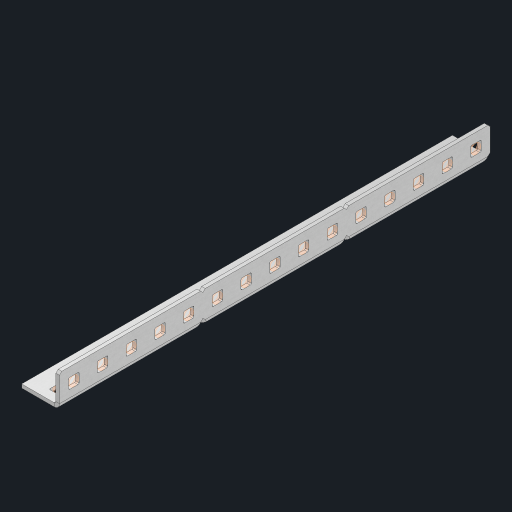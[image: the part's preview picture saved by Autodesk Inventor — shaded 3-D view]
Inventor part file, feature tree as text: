
AUTODESK INVENTOR PART (.ipt)
format: ipt  version: 2023 (Build 270158000, 158)  size: 680,960 bytes
history: native  units: in
note: dims shown in document units (in); Inventor stores cm internally (conversion verified against a paired STEP export)
features: other x35, extrude x29, sheet_metal_op x10, sketch x8, mirror x1, pattern_linear x1, chamfer x1
ambient origin geometry x8: Origin, YZ Plane, XZ Plane, XY Plane, X Axis, Y Axis, Z Axis, Center Point
bodies: Solid1 (feature_tree), Body (feature_tree)
feature tree (85):
  other  "Flange Pattern Plane"
  sheet_metal_op  "Flange Pattern"
  sheet_metal_op  "Body Pattern"
  other  "Arc Length"
  mirror  "Notch Mirror"
  pattern_linear  "Notch Pattern"  Spacing1=0.25in  [1 undecoded]
  chamfer  "End Chamfer"
  extrude  "Half Cut"  Depth=0.0625in
  sketch  "Sketch1"  dims[d0=1.5in]
  other  "Plate1"
  sketch  "Sketch2"  dims[d1=7.5in]
  other  "Plate2"
  sheet_metal_op  "Bend1"
  sheet_metal_op  "Corner1"
  sketch  "Sketch3"  dims[d2=0.0625in]
  other  "Flange Pattern Sketch"
  sketch  "Sketch7"  dims[d3=0.0625in]
  other  "Srf1"
  other  "Srf2"
  sketch  "Sketch8"  dims[d4=0.0312in]
  sketch  "Sketch9"  dims[d5=0.125in]
  other  "Srf91"
  sheet_metal_op  "Body Pattern Sketch"
  other  "Srf92"
  sketch  "Sketch13"  dims[d6=0.0625in]
  sketch  "Sketch14"  dims[d7=0.5in d8=90.0deg d9=0.0312in d10=0.25in d11=0.0625in d12=0.0625in d16=0.182in d17=0.02in d18=0.0625in d19=0.0in d20=0.25in d21=0.25in d46=0.172in d47=1.0in d48=0.0in d49=0.182in d50=0.02in d51=0.25in d52=0.25in d53=0.0625in d54=0.0in d55=0.172in d56=1.0in d57=0.0in d60=5.9055in d62=0.5in d63=0.3937in d65=0.5in d85=0.1473in d86=0.1782in d88=0.04in d89=0.0625in d90=0.0in d91=0.04in d92=0.0491in d95=2.5in d96=0.04in d97=0.25in d98=45.0deg d101=0.0in d102=2.497in d131=0.5in d132=5.9055in d134=0.5in d139=0.5in]
  other  "Srf856"
  other  "Srf1310"
  other  "Srf1311"
  other  "Srf1312"
  other  "Srf1376"
  other  "Srf1377"
  other  "Srf1728"
  other  "Srf1755"
  other  "Srf1878"
  other  "Srf1879"
  other  "Srf1880"
  other  "Srf1881"
  other  "Srf1882"
  other  "Srf1883"
  other  "Srf1884"
  other  "Srf1885"
  other  "Srf1886"
  other  "Srf1942"
  other  "Srf1943"
  other  "Srf1944"
  other  "Srf1945"
  other  "Srf1946"
  other  "Srf1947"
  other  "Srf1948"
  other  "Srf1949"
  other  "Srf1950"
  sheet_metal_op  "Flange Stamp"
  sheet_metal_op  "Flange Circle"
  sheet_metal_op  "Body Stamp"
  sheet_metal_op  "Body Circle"
  sheet_metal_op  "Notch"
  extrude  "ExtrusionSrf2"  Depth=0.0625in
  extrude  "ExtrusionSrf92"  Depth=0.0625in
  extrude  "ExtrusionSrf856"  Depth=0.02in
  extrude  "ExtrusionSrf1310"  Depth=0.0625in
  extrude  "ExtrusionSrf1311"  TaperAngle=0.0deg  [1 undecoded]
  extrude  "ExtrusionSrf1312"  Depth=0.0625in
  extrude  "ExtrusionSrf1376"  Depth=0.0625in
  extrude  "ExtrusionSrf1377"  Depth=0.0625in
  extrude  "ExtrusionSrf1728"  Depth=0.0625in TaperAngle=0.0deg
  extrude  "ExtrusionSrf1755"  Depth=0.0625in
  extrude  "ExtrusionSrf1878"  Depth=0.02in
  extrude  "ExtrusionSrf1879"  Depth=0.0625in
  extrude  "ExtrusionSrf1880"  Depth=0.0625in
  extrude  "ExtrusionSrf1881"  Depth=0.0625in
  extrude  "ExtrusionSrf1882"  TaperAngle=0.0deg  [1 undecoded]
  extrude  "ExtrusionSrf1883"  Depth=0.0625in
  extrude  "ExtrusionSrf1884"  Depth=0.0625in TaperAngle=0.0deg
  extrude  "ExtrusionSrf1885"  Depth=0.0625in
  extrude  "ExtrusionSrf1886"  Depth=0.3937in
  extrude  "ExtrusionSrf1942"  Depth=0.0625in
  extrude  "ExtrusionSrf1943"  Depth=0.0625in
  extrude  "ExtrusionSrf1944"  Depth=0.0625in
  extrude  "ExtrusionSrf1945"  Depth=0.0625in
  extrude  "ExtrusionSrf1946"  TaperAngle=0.0deg  [1 undecoded]
  extrude  "ExtrusionSrf1947"  Depth=0.0625in
  extrude  "ExtrusionSrf1948"  Depth=0.0625in
  extrude  "ExtrusionSrf1949"  Depth=0.0625in
  extrude  "ExtrusionSrf1950"  Depth=0.0625in TaperAngle=45.0deg
note: 4 required parameter values undecoded (feature->parameter linkage not recoverable at this tier; creation-order binding heuristic only, values carry confidence <= 0.55)
